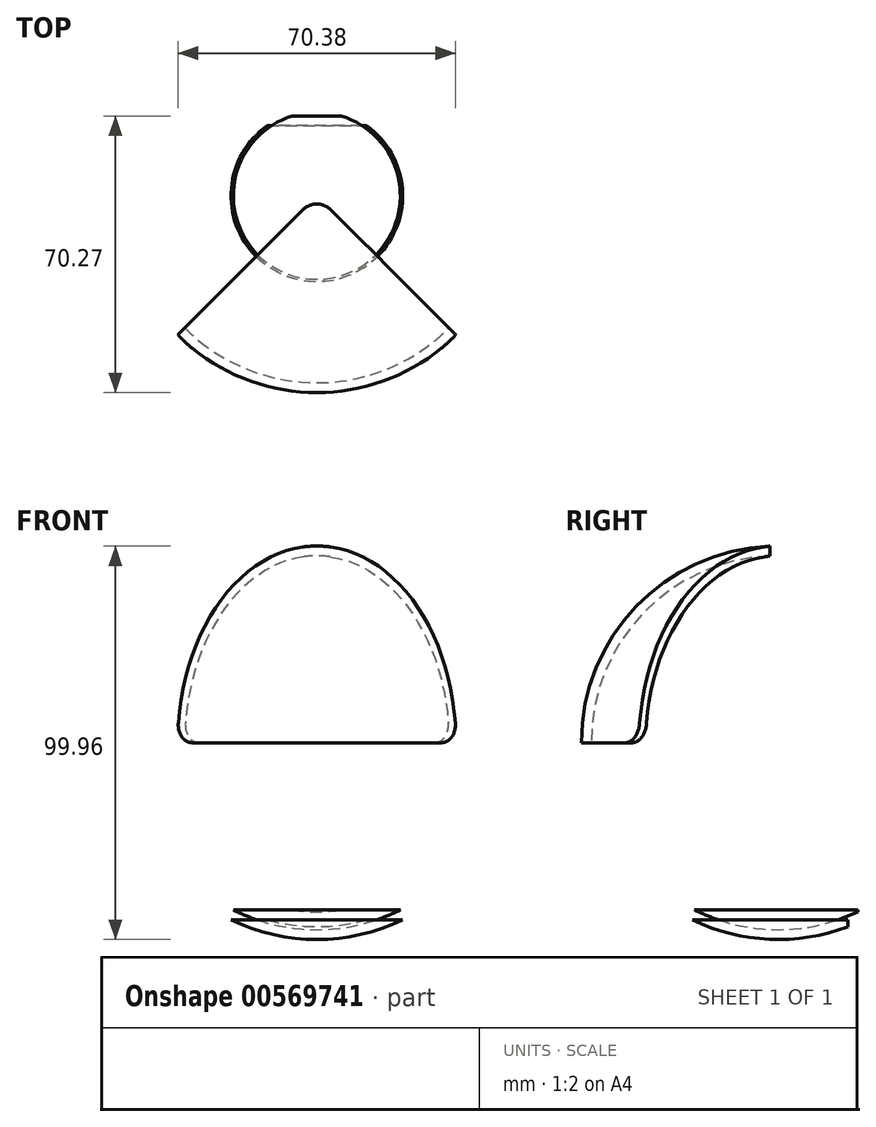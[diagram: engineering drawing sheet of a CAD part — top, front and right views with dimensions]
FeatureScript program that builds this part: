
annotation { "Feature Type Name" : "Feature", "Feature Type Description" : "" }
export const myFeature = defineFeature(function(context is Context, id is Id, definition is map)
    precondition{}
    {
        {
            var Q0;
            Q0=qCreatedBy(makeId("Top.planeOp"),FACE);
            var sketch = newSketch(context, id + "F0", { "sketchPlane" : qUnion([Q0])});
            skArc(sketch, "E0", {"start": v(0, -50) * mm, "mid": v(50, 0) * mm, "end": v(0, 50) * mm});
            skLineSegment(sketch, "E1", {"start": v(0, 50) * mm, "end": v(0, -50) * mm});
            skSolve(sketch);
        }
        {
            var Q0;
            Q0 = qSketchRegion(id + "F0", true);
            var Q1;
            Q1=sQuery(id+"F0.wireOp",EDGE,"E1");
            revolve(context, id + "F1", {"entities" : qUnion([Q0]), "axis" : qUnion([Q1]), "revolveType" : RevolveType.FULL});
        }
        {
            var Q0;
            Q0=qCreatedBy(makeId("Right.planeOp"),FACE);
            var sketch = newSketch(context, id + "F2", { "sketchPlane" : qUnion([Q0])});
            skArc(sketch, "E2", {"start": v(0, 50) * mm, "mid": v(-35.36, 35.36) * mm, "end": v(-50, 0) * mm});
            skLineSegment(sketch, "E3", {"start": v(0, 0) * mm, "end": v(0, 50) * mm});
            skLineSegment(sketch, "E4", {"start": v(0, 0) * mm, "end": v(-50, 0) * mm});
            skSolve(sketch);
        }
        {
            var Q0;
            Q0 = qSketchRegion(id + "F2", true);
            var Q1;
            Q1=sQuery(id+"F2.wireOp",EDGE,"E3");
            revolve(context, id + "F3", {"operationType" : NewBodyOperationType.REMOVE, "entities" : qUnion([Q0]), "axis" : qUnion([Q1]), "revolveType" : RevolveType.SYMMETRIC, "oppositeDirection" : true, "angle" : 90 * degree});
        }
        {
            var Q0;
            Q0=qCreatedBy(makeId("Top.planeOp"),FACE);
            cPlane(context, id + "F4", {"entities" : qUnion([Q0]), "cplaneType" : CPlaneType.OFFSET, "offset" : 50 * mm, "oppositeDirection" : true, "width" : 150 * mm, "height" : 150 * mm});
        }
        {
            var Q0;
            Q0=qCreatedBy(id+"F4.planeOp",FACE);
            var sketch = newSketch(context, id + "F5", { "sketchPlane" : qUnion([Q0])});
            skLineSegment(sketch, "E5.bottom", {"start": v(22.5, 17.77) * mm, "end": v(-27.5, 17.77) * mm});
            skLineSegment(sketch, "E5.top", {"start": v(22.5, -32.23) * mm, "end": v(-27.5, -32.23) * mm});
            skLineSegment(sketch, "E5.left", {"start": v(22.5, 17.77) * mm, "end": v(22.5, -32.23) * mm});
            skLineSegment(sketch, "E5.right", {"start": v(-27.5, 17.77) * mm, "end": v(-27.5, -32.23) * mm});
            skPoint(sketch, "E5.middle", {"position": v(-2.5, -7.23) * mm});
            skSolve(sketch);
        }
        {
            var Q0;
            Q0 = qSketchRegion(id + "F5", true);
            extrude(context, id + "F6", {"entities" : qUnion([Q0]), "operationType" : NewBodyOperationType.REMOVE, "depth" : 5 * mm, "offsetDistance" : 25 * mm});
        }
        {
            var Q0;
            Q0=makeQuery(id+"F3.boolean.opBoolean","COPY",FACE,{"derivedFrom":makeQuery(id+"F3.opRevolve","CAP_FACE",FACE,{"disambiguationData":[OSD([sQuery(id+"F2.wireOp",EDGE,"E2"),sQuery(id+"F2.wireOp",EDGE,"E3"),sQuery(id+"F2.wireOp",EDGE,"E4")])],"isStart":false})});
            var Q1;
            Q1=makeQuery(id+"F3.boolean.opBoolean","COPY",FACE,{"derivedFrom":makeQuery(id+"F3.opRevolve","CAP_FACE",FACE,{"disambiguationData":[OSD([sQuery(id+"F2.wireOp",EDGE,"E2"),sQuery(id+"F2.wireOp",EDGE,"E3"),sQuery(id+"F2.wireOp",EDGE,"E4")])],"isStart":true})});
            var Q2;
            Q2=makeQuery(id+"F3.boolean.opBoolean","COPY",FACE,{"derivedFrom":makeQuery(id+"F3.opRevolve","SWEPT_FACE",FACE,{"disambiguationData":[OSD([sQuery(id+"F2.wireOp",EDGE,"E4")])]})});
            shell(context, id + "F7", {"entities" : qUnion([Q0, Q1, Q2]), "thickness" : 2.5 * mm});
        }
        {
            var Q0;
            Q0=makeQuery(id+"F3.boolean.opBoolean","COPY",EDGE,{"derivedFrom":makeQuery(id+"F3.opRevolve","CAP_EDGE",EDGE,{"disambiguationData":[OSD([sQuery(id+"F2.wireOp",EDGE,"E4")])],"isStart":false})});
            var Q1;
            Q1=makeQuery(id+"F3.boolean.opBoolean","COPY",EDGE,{"derivedFrom":makeQuery(id+"F3.opRevolve","CAP_EDGE",EDGE,{"disambiguationData":[OSD([sQuery(id+"F2.wireOp",EDGE,"E3")])],"isStart":true})});
            var Q2;
            Q2=makeQuery(id+"F3.boolean.opBoolean","COPY",EDGE,{"derivedFrom":makeQuery(id+"F3.opRevolve","CAP_EDGE",EDGE,{"disambiguationData":[OSD([sQuery(id+"F2.wireOp",EDGE,"E4")])],"isStart":true})});
            fillet(context, id + "F8", {"entities" : qUnion([Q0, Q1, Q2]), "radius" : 5 * mm, "tangentPropagation" : true, "allowEdgeOverflow" : false});
        }
    });
